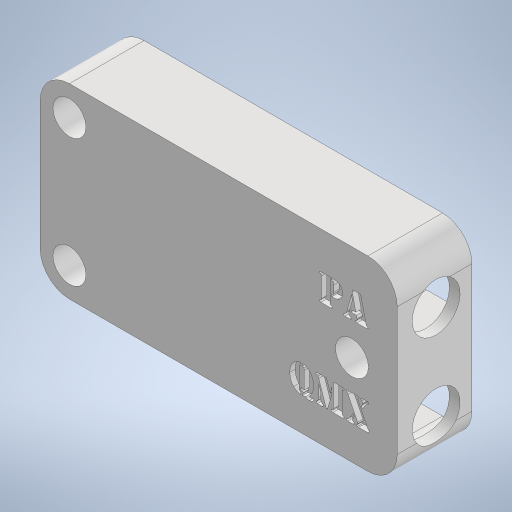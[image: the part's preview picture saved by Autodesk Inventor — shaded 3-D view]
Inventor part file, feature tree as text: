
AUTODESK INVENTOR PART (.ipt)
format: ipt  version: 2023 (Build 270158000, 158)  size: 626,176 bytes
history: native  units: in
note: dims shown in document units (in); Inventor stores cm internally (conversion verified against a paired STEP export)
features: reference x9, sketch x8, extrude x7, projected_geometry x5, other x4, plane x2, fillet x2
ambient origin geometry x8: Origin, YZ Plane, XZ Plane, XY Plane, X Axis, Y Axis, Z Axis, Center Point
bodies: Solid1 (feature_tree)
feature tree (37):
  extrude  "Extrusion1"  Depth=0.315in
  plane  "Work Plane1"
  sketch  "Sketch2"  dims[d3=0.4724in d4=0.0in d5=0.2441in]
  plane  "Work Plane2"
  extrude  "Extrusion2"  Depth=0.2441in
  extrude  "Extrusion3"  Depth=0.2441in
  fillet  "Fillet1"  Radius=0.3937in
  sketch  "Sketch4"  dims[d10=0.0787in d11=0.0787in d12=0.0in]
  sketch  "Sketch5"  dims[d13=0.3543in d14=0.3543in]
  extrude  "Extrusion4"  Depth=0.0787in TaperAngle=0.0deg
  extrude  "Extrusion5"  Depth=0.3543in
  extrude  "Extrusion6"  Depth=0.315in
  fillet  "Fillet2"  Radius=0.5906in
  extrude  "Extrusion7"  Depth=0.0787in
  sketch  "Sketch1"  dims[d0=0.4724in d1=0.0in d2=0.315in]
  reference  "Reference1"
  reference  "Reference2"
  reference  "Reference3"
  reference  "Reference4"
  projected_geometry  "Projected Loop1"
  sketch  "Sketch3"  dims[d6=0.2441in d7=0.2441in d8=0.3937in d9=0.0in]
  projected_geometry  "Projected Loop2"
  projected_geometry  "Projected Loop3"
  projected_geometry  "Projected Loop4"
  projected_geometry  "Projected Loop5"
  sketch  "Sketch6"  dims[d15=0.2338in d16=0.0in d17=0.315in d18=0.5906in]
  reference  "Reference5"
  reference  "Reference6"
  sketch  "Sketch7"  dims[d19=0.4537in d20=0.0in d21=0.0787in]
  reference  "Reference7"
  reference  "Reference8"
  reference  "Reference9"
  sketch  "Sketch8"  dims[d22=0.0394in d23=0.0in]
  other  "<userpath>\Nextcloud2\private\HAMpower\Case\case_assambly.iam"
  other  "case_assambly.iam"
  other  "case_base:1"
  other  "powerplay:1"
